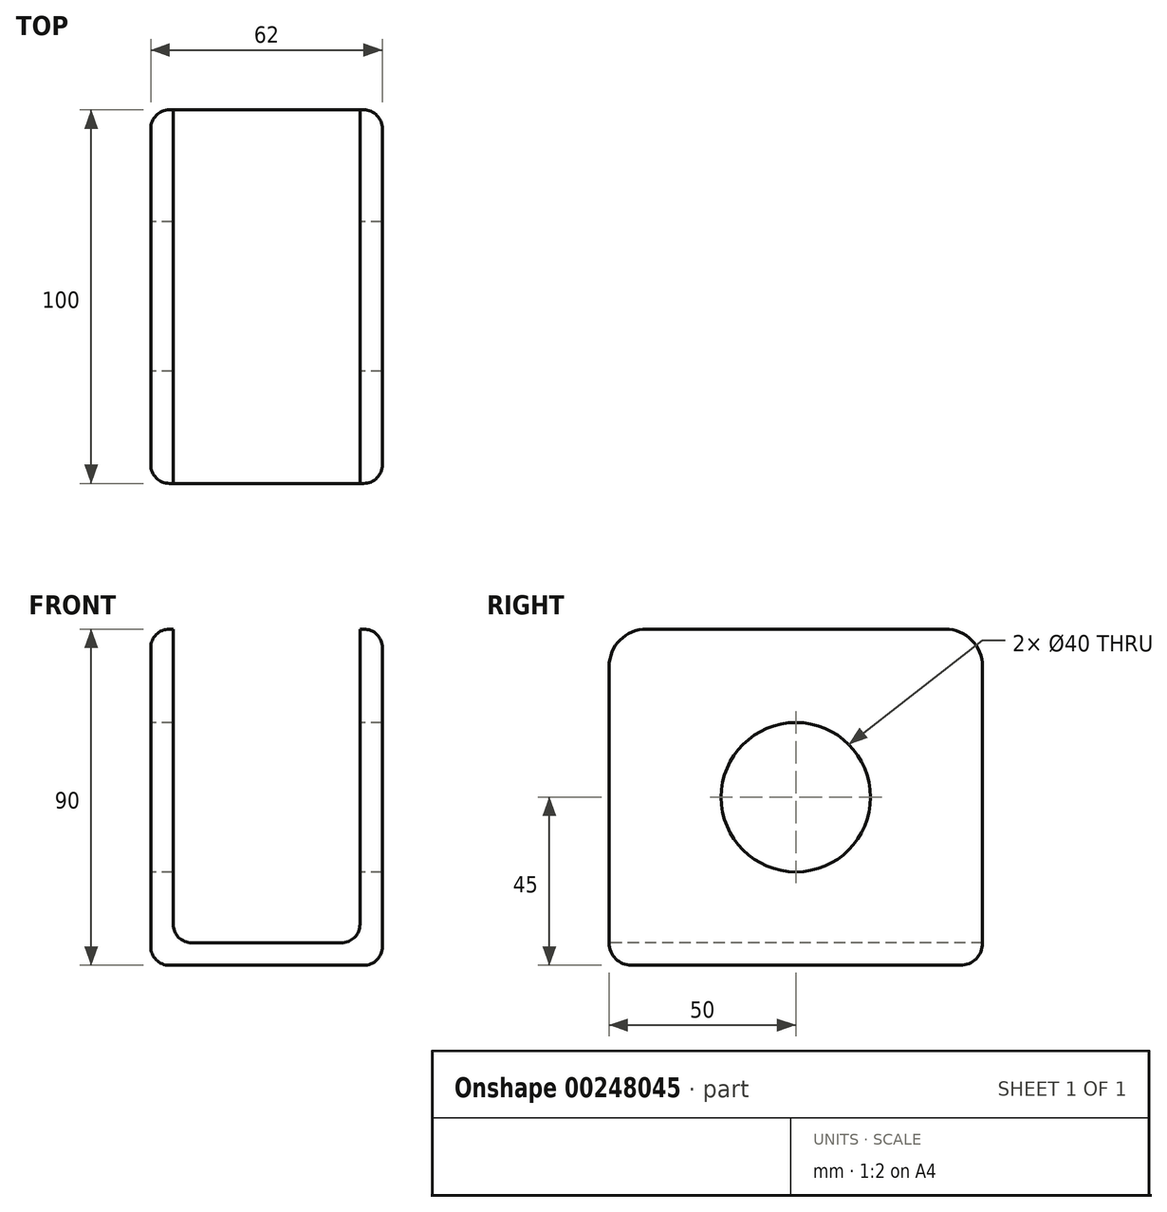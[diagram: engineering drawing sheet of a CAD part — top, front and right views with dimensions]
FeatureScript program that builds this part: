
annotation { "Feature Type Name" : "Feature", "Feature Type Description" : "" }
export const myFeature = defineFeature(function(context is Context, id is Id, definition is map)
    precondition{}
    {
        {
            var Q0;
            Q0=qCreatedBy(makeId("Right.planeOp"),FACE);
            var sketch = newSketch(context, id + "F0", { "sketchPlane" : qUnion([Q0])});
            skLineSegment(sketch, "E0.bottom", {"start": v(44, -45) * mm, "end": v(-44, -45) * mm});
            skLineSegment(sketch, "E0.top", {"start": v(40, 45) * mm, "end": v(-40, 45) * mm});
            skLineSegment(sketch, "E0.left", {"start": v(50, -39) * mm, "end": v(50, -32.43) * mm});
            skLineSegment(sketch, "E0.right", {"start": v(-50, -39) * mm, "end": v(-50, -32.43) * mm});
            skPoint(sketch, "E0.middle", {"position": v(0, 0) * mm});
            skPoint(sketch, "E1", {"position": v(-50, 45) * mm});
            skPoint(sketch, "E2", {"position": v(50, 45) * mm});
            skPoint(sketch, "E3", {"position": v(-50, -30) * mm});
            skPoint(sketch, "E4", {"position": v(50, -30) * mm});
            skLineSegment(sketch, "E5", {"start": v(-50, 35) * mm, "end": v(-50, -32.43) * mm});
            skLineSegment(sketch, "E6", {"start": v(50, 35) * mm, "end": v(50, -32.43) * mm});
            skArc(sketch, "E7.filletArc", {"start": v(-40, 45) * mm, "mid": v(-47.07, 42.07) * mm, "end": v(-50, 35) * mm});
            skArc(sketch, "E8.filletArc", {"start": v(50, 35) * mm, "mid": v(47.07, 42.07) * mm, "end": v(40, 45) * mm});
            skLineSegment(sketch, "E9.filletArc", {"start": v(50, -32.43) * mm, "end": v(50, -32.43) * mm});
            skLineSegment(sketch, "E10.filletArc", {"start": v(-50, -32.43) * mm, "end": v(-50, -32.43) * mm});
            skPoint(sketch, "E11.visualSharp", {"position": v(-50, -45) * mm});
            skArc(sketch, "E11.filletArc", {"start": v(-50, -39) * mm, "mid": v(-48.24, -43.24) * mm, "end": v(-44, -45) * mm});
            skPoint(sketch, "E12.visualSharp", {"position": v(50, -45) * mm});
            skArc(sketch, "E12.filletArc", {"start": v(44, -45) * mm, "mid": v(48.24, -43.24) * mm, "end": v(50, -39) * mm});
            skSolve(sketch);
        }
        {
            var Q0;
            Q0=makeQuery(id+"F0.imprint","IMPRINT",FACE,{"disambiguationData":[TD([[makeQuery(id+"F0.imprint","IMPRINT",EDGE,{"derivedFrom":sQuery(id+"F0.wireOp",EDGE,"E0.bottom")}),-1.0]])]});
            extrude(context, id + "F1", {"entities" : qUnion([Q0]), "depth" : 62 * mm});
        }
        {
            var Q0;
            Q0=makeQuery(id+"F1.opExtrude","SWEPT_FACE",FACE,{"disambiguationData":[OSD([sQuery(id+"F0.wireOp",EDGE,"E0.top")])]});
            var Q1;
            Q1=makeQuery(id+"F1.opExtrude","SWEPT_FACE",FACE,{"disambiguationData":[OSD([sQuery(id+"F0.wireOp",EDGE,"E6")])]});
            var Q2;
            Q2=makeQuery(id+"F1.opExtrude","SWEPT_FACE",FACE,{"disambiguationData":[OSD([sQuery(id+"F0.wireOp",EDGE,"E8.filletArc")])]});
            var Q3;
            Q3=makeQuery(id+"F1.opExtrude","SWEPT_FACE",FACE,{"disambiguationData":[OSD([sQuery(id+"F0.wireOp",EDGE,"E7.filletArc")])]});
            var Q4;
            Q4=makeQuery(id+"F1.opExtrude","SWEPT_FACE",FACE,{"disambiguationData":[OSD([sQuery(id+"F0.wireOp",EDGE,"E5")])]});
            var Q5;
            Q5=makeQuery(id+"F1.opExtrude","SWEPT_FACE",FACE,{"disambiguationData":[OSD([sQuery(id+"F0.wireOp",EDGE,"E9.filletArc")])]});
            var Q6;
            Q6=makeQuery(id+"F1.opExtrude","SWEPT_FACE",FACE,{"disambiguationData":[OSD([sQuery(id+"F0.wireOp",EDGE,"E0.left")])]});
            var Q7;
            Q7=makeQuery(id+"F1.opExtrude","SWEPT_FACE",FACE,{"disambiguationData":[OSD([sQuery(id+"F0.wireOp",EDGE,"E10.filletArc")])]});
            var Q8;
            Q8=makeQuery(id+"F1.opExtrude","SWEPT_FACE",FACE,{"disambiguationData":[OSD([sQuery(id+"F0.wireOp",EDGE,"E0.right")])]});
            shell(context, id + "F2", {"entities" : qUnion([Q0, Q1, Q2, Q3, Q4, Q5, Q6, Q7, Q8]), "thickness" : 6 * mm});
        }
        {
            var Q0;
            Q0=sQuery(id+"F0.wireOp",VERTEX,"E0.middle");
            var Q1;
            Q1=makeQuery(id+"F1.opExtrude","SWEPT_BODY",BODY,{"disambiguationData":[OSD([sQuery(id+"F0.wireOp",EDGE,"E0.bottom"),sQuery(id+"F0.wireOp",EDGE,"E0.top"),sQuery(id+"F0.wireOp",EDGE,"E0.left"),sQuery(id+"F0.wireOp",EDGE,"E0.right"),sQuery(id+"F0.wireOp",EDGE,"E5"),sQuery(id+"F0.wireOp",EDGE,"E6"),sQuery(id+"F0.wireOp",EDGE,"E7.filletArc"),sQuery(id+"F0.wireOp",EDGE,"E8.filletArc"),sQuery(id+"F0.wireOp",EDGE,"E9.filletArc"),sQuery(id+"F0.wireOp",EDGE,"E10.filletArc"),sQuery(id+"F0.wireOp",EDGE,"E11.filletArc"),sQuery(id+"F0.wireOp",EDGE,"E12.filletArc")])]});
            hole(context, id + "F3", {"style" : HoleStyle.SIMPLE, "endStyle" : HoleEndStyle.THROUGH, "oppositeDirection" : true, "holeDiameter" : 40 * mm, "tappedDepth" : 12 * mm, "tapClearance" : 3, "locations" : qUnion([Q0]), "scope" : qUnion([Q1])});
        }
        {
            var Q0;
            {var subQ0=sQuery(id+"F0.wireOp",EDGE,"E0.bottom");Q0=makeQuery(id+"F2.opShell","OFFSET_EDGE",EDGE,{"disambiguationData":[OSD([subQ0]),TDD([makeQuery(id+"F1.opExtrude","CAP_EDGE",EDGE,{"disambiguationData":[OSD([subQ0])],"isStart":true})])]});}
            var Q1;
            {var subQ0=sQuery(id+"F0.wireOp",EDGE,"E0.bottom");Q1=makeQuery(id+"F2.opShell","OFFSET_EDGE",EDGE,{"disambiguationData":[OSD([subQ0]),TDD([makeQuery(id+"F1.opExtrude","CAP_EDGE",EDGE,{"disambiguationData":[OSD([subQ0])],"isStart":false})])]});}
            fillet(context, id + "F4", {"entities" : qUnion([Q0, Q1]), "radius" : 5 * mm, "tangentPropagation" : true, "allowEdgeOverflow" : false});
        }
        {
            var Q0;
            Q0=makeQuery(id+"F1.opExtrude","CAP_EDGE",EDGE,{"disambiguationData":[OSD([sQuery(id+"F0.wireOp",EDGE,"E0.bottom")])],"isStart":false});
            var Q1;
            Q1=makeQuery(id+"F1.opExtrude","CAP_EDGE",EDGE,{"disambiguationData":[OSD([sQuery(id+"F0.wireOp",EDGE,"E0.bottom")])],"isStart":true});
            fillet(context, id + "F5", {"entities" : qUnion([Q0, Q1]), "radius" : 5 * mm, "tangentPropagation" : true, "allowEdgeOverflow" : false});
        }
    });
